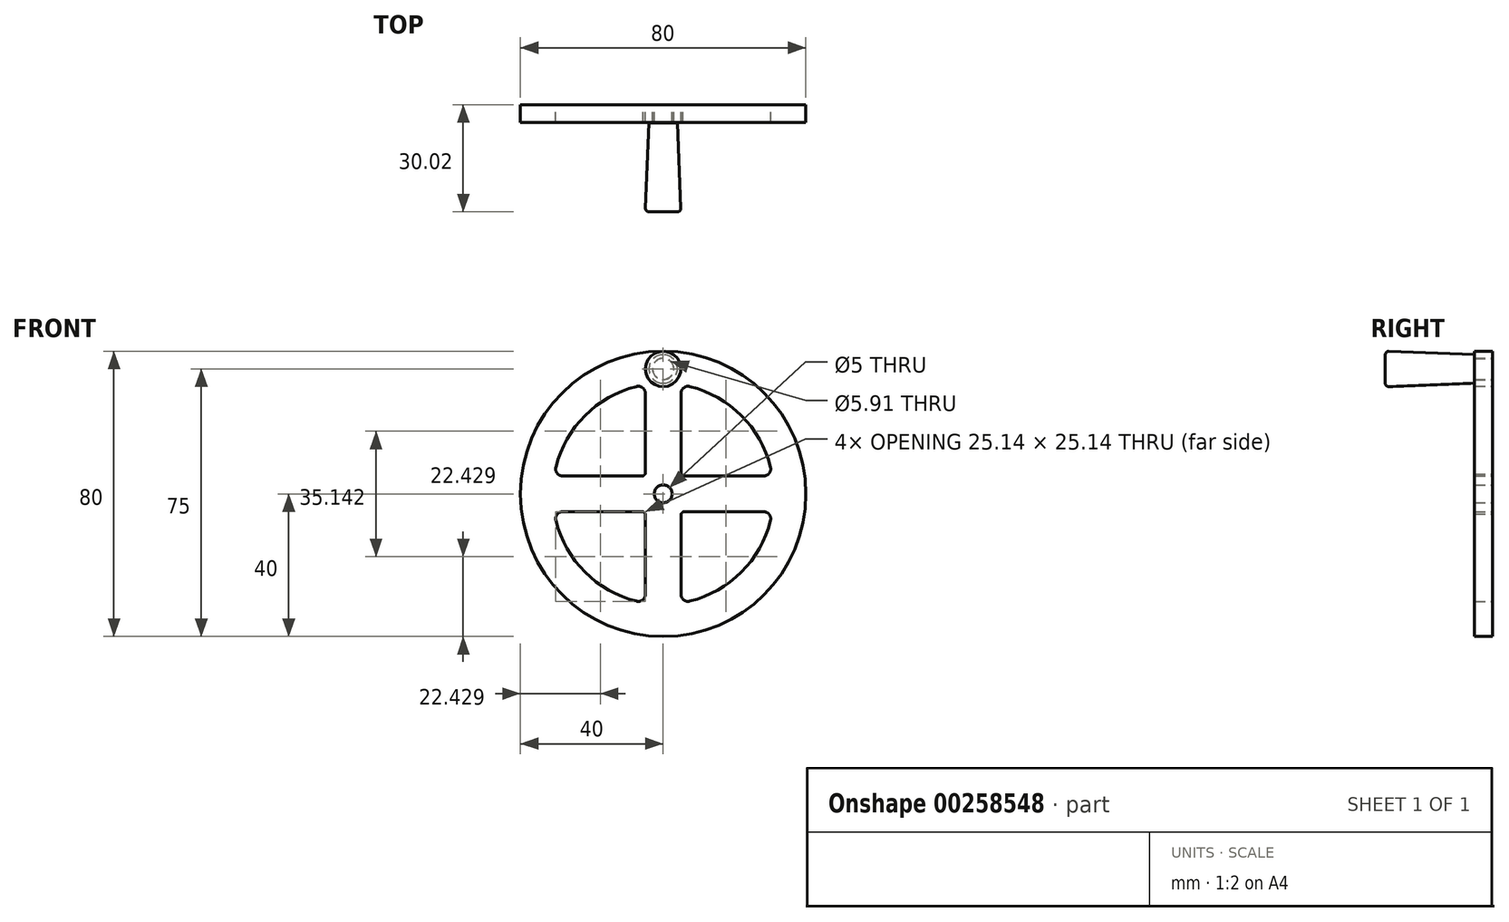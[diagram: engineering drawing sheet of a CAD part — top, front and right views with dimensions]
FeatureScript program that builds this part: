
annotation { "Feature Type Name" : "Feature", "Feature Type Description" : "" }
export const myFeature = defineFeature(function(context is Context, id is Id, definition is map)
    precondition{}
    {
        {
            var Q0;
            Q0=qCreatedBy(makeId("Right.planeOp"),FACE);
            var sketch = newSketch(context, id + "F0", { "sketchPlane" : qUnion([Q0])});
            skLineSegment(sketch, "E0", {"start": v(2.38, 35) * mm, "end": v(-31.09, 35) * mm, "construction": true});
            skLineSegment(sketch, "E1", {"start": v(-30.02, 40) * mm, "end": v(-5.02, 39) * mm});
            skLineSegment(sketch, "E2", {"start": v(-30.02, 40) * mm, "end": v(-30.02, 35) * mm});
            skPoint(sketch, "E3.orphan", {"position": v(-30.02, 30) * mm});
            skLineSegment(sketch, "E4", {"start": v(-5.02, 39) * mm, "end": v(-5.02, 35) * mm});
            skLineSegment(sketch, "E5", {"start": v(-30.02, 35) * mm, "end": v(-5.02, 35) * mm});
            skLineSegment(sketch, "E6.bottom", {"start": v(-5.02, 35) * mm, "end": v(0, 35) * mm});
            skLineSegment(sketch, "E6.top", {"start": v(-5.02, 38) * mm, "end": v(0, 38) * mm});
            skLineSegment(sketch, "E6.left", {"start": v(-5.02, 35) * mm, "end": v(-5.02, 38) * mm});
            skLineSegment(sketch, "E6.right", {"start": v(0, 35) * mm, "end": v(0, 38) * mm});
            skSolve(sketch);
        }
        {
            var Q0;
            Q0=makeQuery(id+"F0.imprint","IMPRINT",FACE,{"disambiguationData":[TD([[makeQuery(id+"F0.imprint","IMPRINT",EDGE,{"derivedFrom":sQuery(id+"F0.wireOp",EDGE,"E6.bottom")}),1.0]])]});
            var Q1;
            Q1=makeQuery(id+"F0.imprint","IMPRINT",FACE,{"disambiguationData":[TD([[makeQuery(id+"F0.imprint","IMPRINT",EDGE,{"derivedFrom":sQuery(id+"F0.wireOp",EDGE,"E1")}),-1.0]])]});
            var Q2;
            Q2=sQuery(id+"F0.wireOp",EDGE,"E0");
            revolve(context, id + "F1", {"entities" : qUnion([Q0, Q1]), "axis" : qUnion([Q2]), "revolveType" : RevolveType.FULL});
        }
        {
            var Q0;
            Q0=makeQuery(id+"F1.opRevolve","SWEPT_EDGE",EDGE,{"disambiguationData":[OSD([sQuery(id+"F0.wireOp",EDGE,"E1"),sQuery(id+"F0.wireOp",EDGE,"E2")])]});
            fillet(context, id + "F2", {"entities" : qUnion([Q0]), "radius" : 1 * mm, "tangentPropagation" : true, "allowEdgeOverflow" : false});
        }
        {
            var Q0;
            Q0=qCreatedBy(makeId("Front.planeOp"),FACE);
            var sketch = newSketch(context, id + "F3", { "sketchPlane" : qUnion([Q0])});
            skCircle(sketch, "E7", {"center": v(0, 0) * mm, "radius": 40 * mm});
            skArc(sketch, "E8", {"start": v(30.6, 5) * mm, "mid": v(21.92, 21.92) * mm, "end": v(5, 30.6) * mm});
            skArc(sketch, "E9", {"start": v(5.6, 5) * mm, "mid": v(5.3, 5.3) * mm, "end": v(5, 5.6) * mm});
            skCircle(sketch, "E10", {"center": v(0, 0) * mm, "radius": 2.5 * mm});
            skLineSegment(sketch, "E11", {"start": v(0, 0) * mm, "end": v(0, 40) * mm, "construction": true});
            skLineSegment(sketch, "E12", {"start": v(0, 0) * mm, "end": v(2.5, 0) * mm});
            skLineSegment(sketch, "E13", {"start": v(0, 0) * mm, "end": v(-2.5, 0) * mm});
            skLineSegment(sketch, "E14", {"start": v(0, 0) * mm, "end": v(0, -40) * mm, "construction": true});
            skLineSegment(sketch, "E15.0", {"start": v(5, 5.6) * mm, "end": v(5, 30.6) * mm});
            skLineSegment(sketch, "E16.0", {"start": v(-5, 5.6) * mm, "end": v(-5, 30.6) * mm});
            skLineSegment(sketch, "E17.0", {"start": v(5.6, -5) * mm, "end": v(30.6, -5) * mm});
            skLineSegment(sketch, "E18.0", {"start": v(5.6, 5) * mm, "end": v(30.6, 5) * mm});
            skLineSegment(sketch, "E19.0", {"start": v(-5, -5.6) * mm, "end": v(-5, -30.6) * mm});
            skLineSegment(sketch, "E20.0", {"start": v(-5.6, -5) * mm, "end": v(-30.6, -5) * mm});
            skLineSegment(sketch, "E21.0", {"start": v(-5.6, 5) * mm, "end": v(-30.6, 5) * mm});
            skLineSegment(sketch, "E22.0", {"start": v(5, -5.6) * mm, "end": v(5, -30.6) * mm});
            skArc(sketch, "E23.trimOffspring", {"start": v(5, -30.6) * mm, "mid": v(21.92, -21.92) * mm, "end": v(30.6, -5) * mm});
            skArc(sketch, "E24.trimOffspring", {"start": v(-30.6, -5) * mm, "mid": v(-21.92, -21.92) * mm, "end": v(-5, -30.6) * mm});
            skArc(sketch, "E25.trimOffspring", {"start": v(-5, 30.6) * mm, "mid": v(-21.92, 21.92) * mm, "end": v(-30.6, 5) * mm});
            skArc(sketch, "E26.trimOffspring", {"start": v(-5, 5.6) * mm, "mid": v(-5.3, 5.3) * mm, "end": v(-5.6, 5) * mm});
            skArc(sketch, "E27.trimOffspring", {"start": v(-5.6, -5) * mm, "mid": v(-5.3, -5.3) * mm, "end": v(-5, -5.6) * mm});
            skArc(sketch, "E28.trimOffspring", {"start": v(5, -5.6) * mm, "mid": v(5.3, -5.3) * mm, "end": v(5.6, -5) * mm});
            skLineSegment(sketch, "E29", {"start": v(0, 0) * mm, "end": v(30.94, 0) * mm, "construction": true});
            skLineSegment(sketch, "E30", {"start": v(0, 0) * mm, "end": v(-29.2, 0) * mm, "construction": true});
            skCircle(sketch, "E31", {"center": v(0, 35) * mm, "radius": 2.95 * mm});
            skSolve(sketch);
        }
        {
            var Q0;
            Q0=makeQuery(id+"F3.imprint","IMPRINT",FACE,{"disambiguationData":[TD([[makeQuery(id+"F3.imprint","IMPRINT",EDGE,{"derivedFrom":sQuery(id+"F3.wireOp",EDGE,"E7")}),1.0]])]});
            var Q1;
            Q1=sQuery(id+"F3.wireOp",EDGE,"E11");
            var Q2;
            Q2=sQuery(id+"F3.wireOp",EDGE,"E30");
            var Q3;
            Q3=sQuery(id+"F3.wireOp",EDGE,"E29");
            var Q4;
            Q4=sQuery(id+"F3.wireOp",EDGE,"E14");
            extrude(context, id + "F4", {"entities" : qUnion([Q0]), "surfaceEntities" : qUnion([Q1, Q2, Q3, Q4]), "depth" : 5 * mm});
        }
        {
            var Q0;
            Q0=makeQuery(id+"F4.opExtrude","SWEPT_EDGE",EDGE,{"disambiguationData":[OSD([sQuery(id+"F3.wireOp",EDGE,"E8"),sQuery(id+"F3.wireOp",EDGE,"E15.0")])]});
            var Q1;
            Q1=makeQuery(id+"F4.opExtrude","SWEPT_EDGE",EDGE,{"disambiguationData":[OSD([sQuery(id+"F3.wireOp",EDGE,"E16.0"),sQuery(id+"F3.wireOp",EDGE,"E25.trimOffspring")])]});
            var Q2;
            Q2=makeQuery(id+"F4.opExtrude","SWEPT_EDGE",EDGE,{"disambiguationData":[OSD([sQuery(id+"F3.wireOp",EDGE,"E21.0"),sQuery(id+"F3.wireOp",EDGE,"E25.trimOffspring")])]});
            var Q3;
            Q3=makeQuery(id+"F4.opExtrude","SWEPT_EDGE",EDGE,{"disambiguationData":[OSD([sQuery(id+"F3.wireOp",EDGE,"E20.0"),sQuery(id+"F3.wireOp",EDGE,"E24.trimOffspring")])]});
            var Q4;
            Q4=makeQuery(id+"F4.opExtrude","SWEPT_EDGE",EDGE,{"disambiguationData":[OSD([sQuery(id+"F3.wireOp",EDGE,"E19.0"),sQuery(id+"F3.wireOp",EDGE,"E24.trimOffspring")])]});
            var Q5;
            Q5=makeQuery(id+"F4.opExtrude","SWEPT_EDGE",EDGE,{"disambiguationData":[OSD([sQuery(id+"F3.wireOp",EDGE,"E22.0"),sQuery(id+"F3.wireOp",EDGE,"E23.trimOffspring")])]});
            var Q6;
            Q6=makeQuery(id+"F4.opExtrude","SWEPT_EDGE",EDGE,{"disambiguationData":[OSD([sQuery(id+"F3.wireOp",EDGE,"E17.0"),sQuery(id+"F3.wireOp",EDGE,"E23.trimOffspring")])]});
            var Q7;
            Q7=makeQuery(id+"F4.opExtrude","SWEPT_EDGE",EDGE,{"disambiguationData":[OSD([sQuery(id+"F3.wireOp",EDGE,"E8"),sQuery(id+"F3.wireOp",EDGE,"E18.0")])]});
            fillet(context, id + "F5", {"entities" : qUnion([Q0, Q1, Q2, Q3, Q4, Q5, Q6, Q7]), "radius" : 2 * mm, "tangentPropagation" : true, "allowEdgeOverflow" : false});
        }
    });
